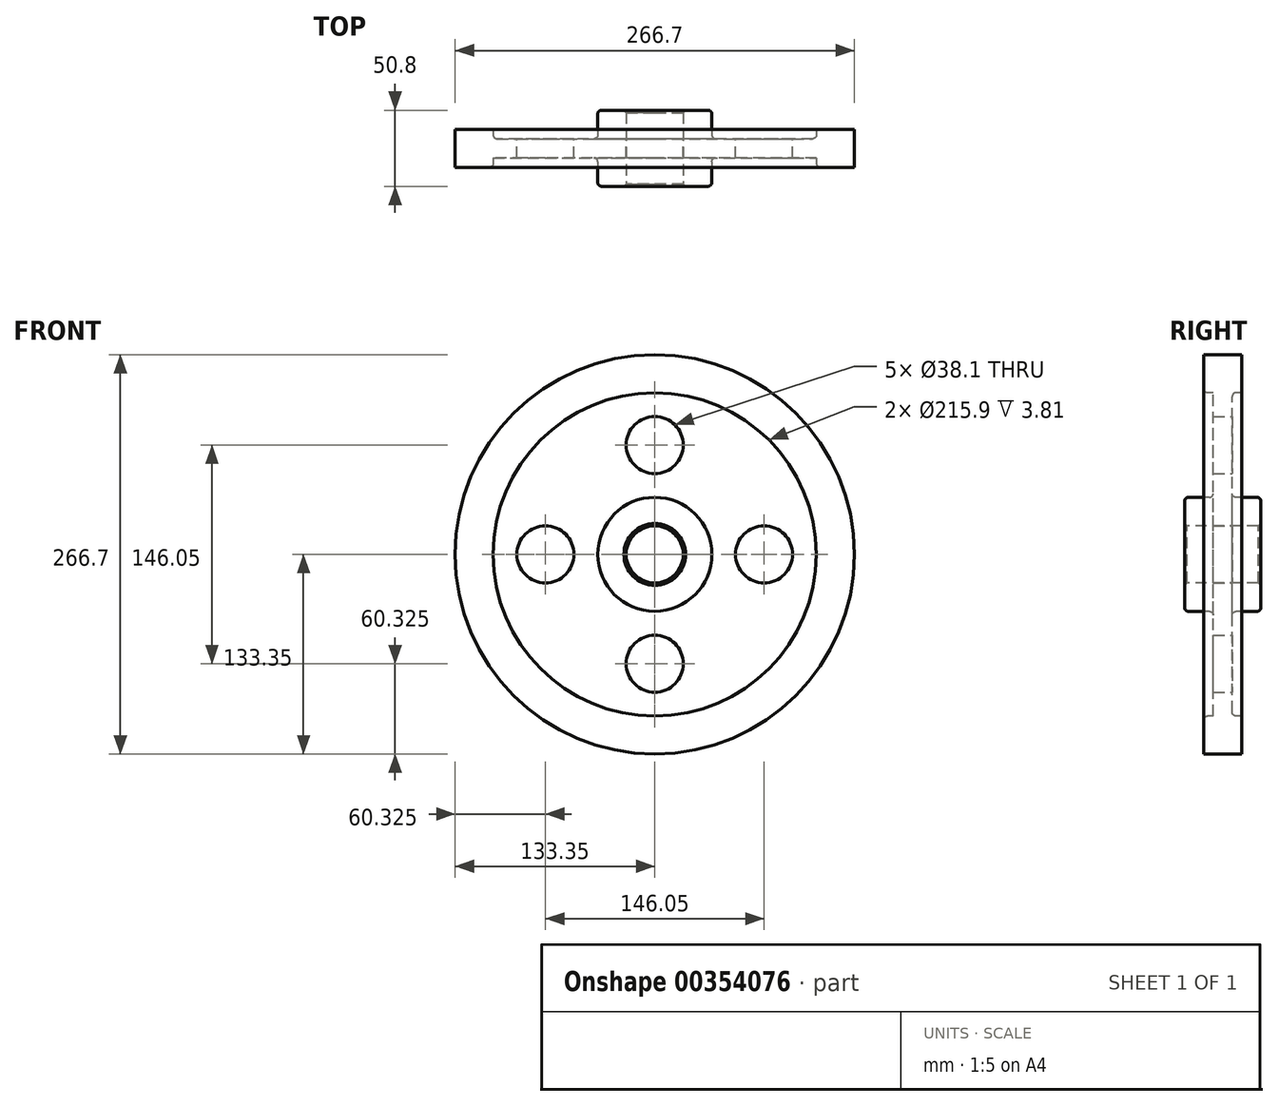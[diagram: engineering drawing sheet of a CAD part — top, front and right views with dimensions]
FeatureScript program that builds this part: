
annotation { "Feature Type Name" : "Feature", "Feature Type Description" : "" }
export const myFeature = defineFeature(function(context is Context, id is Id, definition is map)
    precondition{}
    {
        {
            var Q0;
            Q0=qCreatedBy(makeId("Right.planeOp"),FACE);
            var sketch = newSketch(context, id + "F0", { "sketchPlane" : qUnion([Q0])});
            skLineSegment(sketch, "E0", {"start": v(0, 0) * mm, "end": v(81.69, 0) * mm, "construction": true});
            skLineSegment(sketch, "E1.0", {"start": v(0, 19.05) * mm, "end": v(25.4, 19.05) * mm});
            skLineSegment(sketch, "E2.0", {"start": v(6.35, 38.1) * mm, "end": v(25.4, 38.1) * mm});
            skLineSegment(sketch, "E3.0", {"start": v(6.35, 107.95) * mm, "end": v(12.7, 107.95) * mm});
            skLineSegment(sketch, "E4.0", {"start": v(0, 133.35) * mm, "end": v(12.7, 133.35) * mm});
            skLineSegment(sketch, "E5", {"start": v(0, 0) * mm, "end": v(0, 133.35) * mm, "construction": true});
            skLineSegment(sketch, "E6.0", {"start": v(25.4, 19.05) * mm, "end": v(25.4, 38.1) * mm});
            skLineSegment(sketch, "E7.trimOffspring", {"start": v(12.7, 107.95) * mm, "end": v(12.7, 133.35) * mm});
            skLineSegment(sketch, "E8.trimOffspring", {"start": v(6.35, 38.1) * mm, "end": v(6.35, 107.95) * mm});
            skLineSegment(sketch, "E9.MirrorCS", {"start": v(0, 133.35) * mm, "end": v(-12.7, 133.35) * mm});
            skLineSegment(sketch, "E10.MirrorCS", {"start": v(-12.7, 107.95) * mm, "end": v(-12.7, 133.35) * mm});
            skLineSegment(sketch, "E11.MirrorCS", {"start": v(-6.35, 107.95) * mm, "end": v(-12.7, 107.95) * mm});
            skLineSegment(sketch, "E12.MirrorCS", {"start": v(-6.35, 38.1) * mm, "end": v(-6.35, 107.95) * mm});
            skLineSegment(sketch, "E13.MirrorCS", {"start": v(-6.35, 38.1) * mm, "end": v(-25.4, 38.1) * mm});
            skLineSegment(sketch, "E14.MirrorCS", {"start": v(-25.4, 19.05) * mm, "end": v(-25.4, 38.1) * mm});
            skLineSegment(sketch, "E15.MirrorCS", {"start": v(0, 19.05) * mm, "end": v(-25.4, 19.05) * mm});
            skSolve(sketch);
        }
        {
            var Q0;
            Q0=makeQuery(id+"F0.imprint","IMPRINT",FACE,{"disambiguationData":[TD([[makeQuery(id+"F0.imprint","IMPRINT",EDGE,{"derivedFrom":sQuery(id+"F0.wireOp",EDGE,"E1.0")}),1.0]])]});
            var Q1;
            Q1=sQuery(id+"F0.wireOp",EDGE,"E0");
            revolve(context, id + "F1", {"entities" : qUnion([Q0]), "axis" : qUnion([Q1]), "revolveType" : RevolveType.FULL});
        }
        {
            var Q0;
            Q0=makeQuery(id+"F1.opRevolve","SWEPT_FACE",FACE,{"disambiguationData":[OSD([sQuery(id+"F0.wireOp",EDGE,"E8.trimOffspring")])]});
            var sketch = newSketch(context, id + "F2", { "sketchPlane" : qUnion([Q0])});
            skLineSegment(sketch, "E16", {"start": v(0, 0) * mm, "end": v(0, 73.03) * mm});
            skCircle(sketch, "E17", {"center": v(0, 73.03) * mm, "radius": 19.05 * mm});
            skCircle(sketch, "E18.1.0", {"center": v(-73.03, 0) * mm, "radius": 19.05 * mm});
            skCircle(sketch, "E18.2.0", {"center": v(0, -73.03) * mm, "radius": 19.05 * mm});
            skCircle(sketch, "E18.3.0", {"center": v(73.03, 0) * mm, "radius": 19.05 * mm});
            skPoint(sketch, "E18.center", {"position": v(0, 0) * mm});
            skSolve(sketch);
        }
        {
            var Q0;
            Q0=makeQuery(id+"F2.imprint","IMPRINT",FACE,{"disambiguationData":[TD([[makeQuery(id+"F2.imprint","IMPRINT",EDGE,{"derivedFrom":sQuery(id+"F2.wireOp",EDGE,"E18.1.0")}),1.0]])]});
            var Q1;
            Q1=makeQuery(id+"F2.imprint","IMPRINT",FACE,{"disambiguationData":[TD([[makeQuery(id+"F2.imprint","IMPRINT",EDGE,{"derivedFrom":sQuery(id+"F2.wireOp",EDGE,"E17")}),1.0]])]});
            var Q2;
            Q2=makeQuery(id+"F2.imprint","IMPRINT",FACE,{"disambiguationData":[TD([[makeQuery(id+"F2.imprint","IMPRINT",EDGE,{"derivedFrom":sQuery(id+"F2.wireOp",EDGE,"E18.3.0")}),1.0]])]});
            var Q3;
            Q3=makeQuery(id+"F2.imprint","IMPRINT",FACE,{"disambiguationData":[TD([[makeQuery(id+"F2.imprint","IMPRINT",EDGE,{"derivedFrom":sQuery(id+"F2.wireOp",EDGE,"E18.2.0")}),1.0]])]});
            extrude(context, id + "F3", {"entities" : qUnion([Q0, Q1, Q2, Q3]), "operationType" : NewBodyOperationType.REMOVE, "oppositeDirection" : true, "depth" : 25.4 * mm});
        }
        {
            var Q0;
            Q0=makeQuery(id+"F1.opRevolve","SWEPT_EDGE",EDGE,{"disambiguationData":[OSD([sQuery(id+"F0.wireOp",EDGE,"E2.0"),sQuery(id+"F0.wireOp",EDGE,"E6.0")])]});
            var Q1;
            Q1=makeQuery(id+"F1.opRevolve","SWEPT_EDGE",EDGE,{"disambiguationData":[OSD([sQuery(id+"F0.wireOp",EDGE,"E2.0"),sQuery(id+"F0.wireOp",EDGE,"E8.trimOffspring")])]});
            var Q2;
            Q2=makeQuery(id+"F1.opRevolve","SWEPT_EDGE",EDGE,{"disambiguationData":[OSD([sQuery(id+"F0.wireOp",EDGE,"E3.0"),sQuery(id+"F0.wireOp",EDGE,"E8.trimOffspring")])]});
            var Q3;
            Q3=makeQuery(id+"F1.opRevolve","SWEPT_EDGE",EDGE,{"disambiguationData":[OSD([sQuery(id+"F0.wireOp",EDGE,"E13.MirrorCS"),sQuery(id+"F0.wireOp",EDGE,"E14.MirrorCS")])]});
            var Q4;
            Q4=makeQuery(id+"F1.opRevolve","SWEPT_EDGE",EDGE,{"disambiguationData":[OSD([sQuery(id+"F0.wireOp",EDGE,"E12.MirrorCS"),sQuery(id+"F0.wireOp",EDGE,"E13.MirrorCS")])]});
            var Q5;
            Q5=makeQuery(id+"F1.opRevolve","SWEPT_EDGE",EDGE,{"disambiguationData":[OSD([sQuery(id+"F0.wireOp",EDGE,"E10.MirrorCS"),sQuery(id+"F0.wireOp",EDGE,"E11.MirrorCS")])]});
            fillet(context, id + "F4", {"entities" : qUnion([Q0, Q1, Q2, Q3, Q4, Q5]), "radius" : 2.54 * mm, "tangentPropagation" : true, "allowEdgeOverflow" : false});
        }
        {
            var Q0;
            Q0=makeQuery(id+"F1.opRevolve","SWEPT_EDGE",EDGE,{"disambiguationData":[OSD([sQuery(id+"F0.wireOp",EDGE,"E14.MirrorCS"),sQuery(id+"F0.wireOp",EDGE,"E15.MirrorCS")])]});
            var Q1;
            Q1=makeQuery(id+"F1.opRevolve","SWEPT_EDGE",EDGE,{"disambiguationData":[OSD([sQuery(id+"F0.wireOp",EDGE,"E1.0"),sQuery(id+"F0.wireOp",EDGE,"E6.0")])]});
            chamfer(context, id + "F5", {"entities" : qUnion([Q0, Q1]), "width" : 1.59 * mm, "tangentPropagation" : true});
        }
    });
